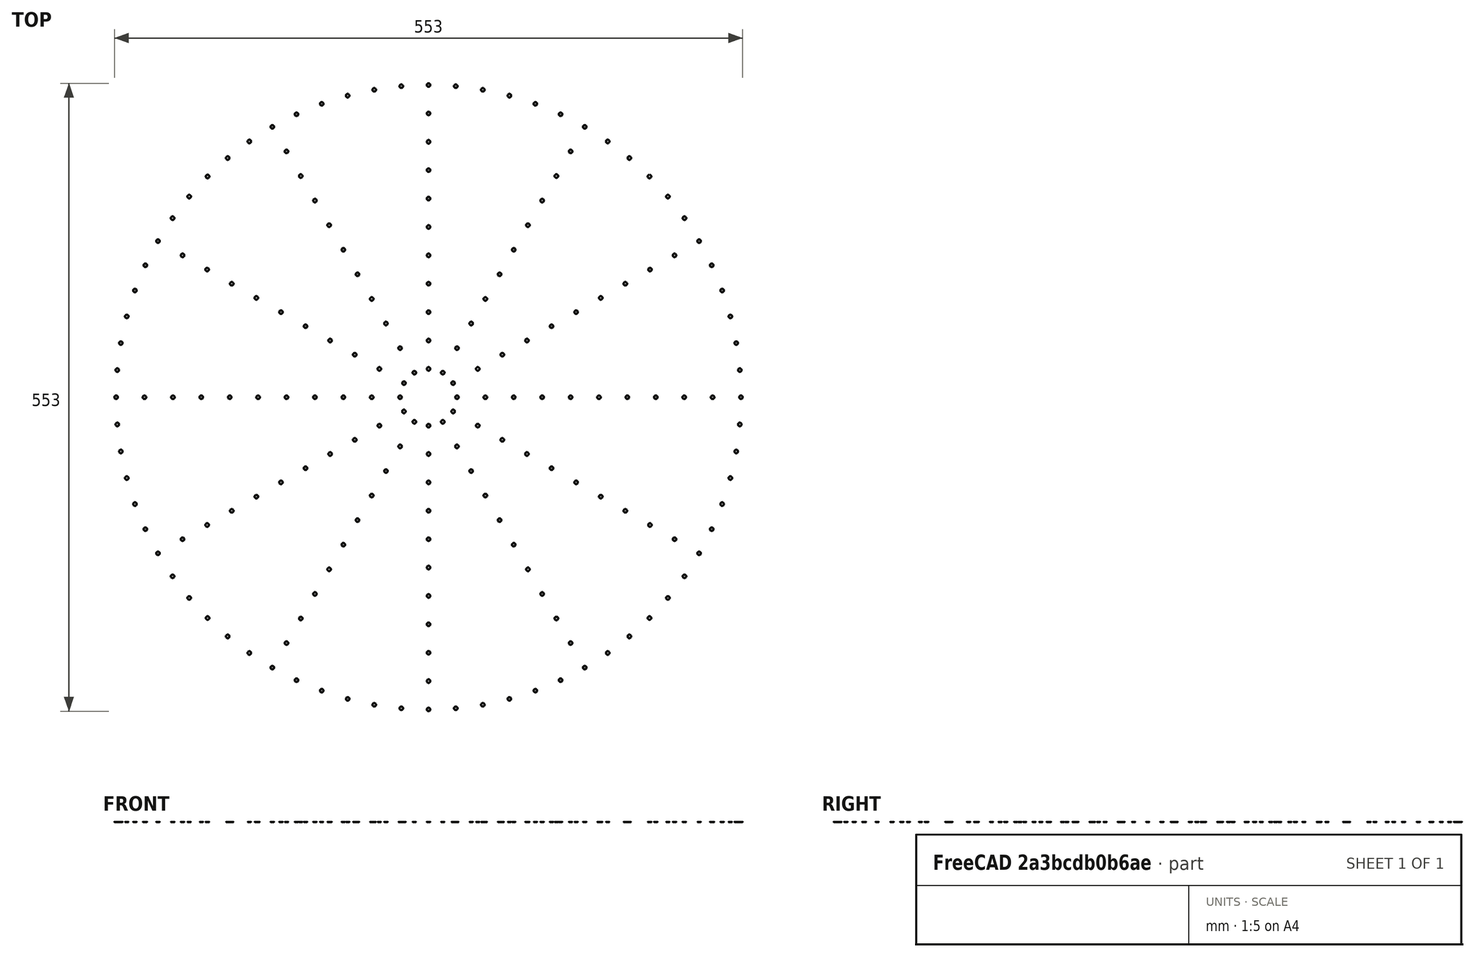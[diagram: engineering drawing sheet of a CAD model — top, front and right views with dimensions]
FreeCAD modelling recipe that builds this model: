
FCSTD DOCUMENT  (FreeCAD 0.16RUnknown)
Label: Wheel
License: All rights reserved
LicenseURL: http://en.wikipedia.org/wiki/All_rights_reserved
objects: Part::Part2DObjectPython×4, Part::FeaturePython×3, Spreadsheet::Sheet×1
note: 7 computed .brp shape members not serialized (recipe doc carries the construction recipe); baked Part::Feature solids carry a one-line shape summary decoded from their .brp

FEATURE [Part::Part2DObjectPython] Circle  label="externalCircle"  # Draft 2D object (typed FeaturePython)
  FirstAngle = 0
  LastAngle = 0
  MakeFace = true
  Radius = 280
  expr: Radius = prefs.circleExternal / 2
FEATURE [Spreadsheet::Sheet] Spreadsheet  label="prefs"
  cells = A1=External circle diameter; B1(circleExternal)=560; C1=mm; D1=name=circleExternal; A2=Holes diameter; B2(holeDiameter)=3; C2=mm; D2=name=holeDiameter; A3=Center hole diameter; B3(centerDiameter)=8; C3=mm; D3=name=circleExternal; A4=External holes diameter; B4(externalHole)=3; C4=mm; D4=name=circleExternal
FEATURE [Part::Part2DObjectPython] Circle001  label="hole"  # Draft 2D object (typed FeaturePython)
  FirstAngle = 0
  LastAngle = 0
  MakeFace = true
  Placement = pos=(0,25,0) rot=(0,0,1;0rad)
  Radius = 1.5
  expr: Radius = prefs.holeDiameter / 2
FEATURE [Part::FeaturePython] Array  label="orthoArray"  # Draft array (typed FeaturePython)
  Angle = 360
  ArrayType = 0
  Axis = (0,0,1)
  Base = -> Circle001
  Center = (0,0,0)
  Fuse = false
  IntervalAxis = (0,0,0)
  IntervalX = (1,0,0)
  IntervalY = (0,25,0)
  IntervalZ = (0,0,0)
  NumberPolar = 1
  NumberX = 1
  NumberY = 10
  NumberZ = 1
FEATURE [Part::Part2DObjectPython] Circle002  label="centerHole"  # Draft 2D object (typed FeaturePython)
  FirstAngle = 0
  LastAngle = 0
  MakeFace = true
  Placement = pos=(0,0,0) rot=(1,0,0;3.14159rad)
  Radius = 4
  expr: Radius = prefs.centerDiameter / 2
FEATURE [Part::Part2DObjectPython] Circle003  label="extHole"  # Draft 2D object (typed FeaturePython)
  FirstAngle = 0
  LastAngle = 0
  MakeFace = true
  Placement = pos=(0,275,0) rot=(1,0,0;3.14159rad)
  Radius = 1.5
  expr: Radius = prefs.externalHole / 2
FEATURE [Part::FeaturePython] Array001  label="extArray"  # Draft array (typed FeaturePython)
  Angle = 360
  ArrayType = 1
  Axis = (0,0,1)
  Base = -> Circle003
  Center = (0,0,0)
  Fuse = false
  IntervalAxis = (0,0,0)
  IntervalX = (1,0,0)
  IntervalY = (0,1,0)
  IntervalZ = (0,0,0)
  NumberPolar = 72
  NumberX = 1
  NumberY = 1
  NumberZ = 1
FEATURE [Part::FeaturePython] Array002  label="intArray"  # Draft array (typed FeaturePython)
  Angle = 360
  ArrayType = 1
  Axis = (0,0,1)
  Base = -> Array
  Center = (0,0,0)
  Fuse = false
  IntervalAxis = (0,0,0)
  IntervalX = (1,0,0)
  IntervalY = (0,1,0)
  IntervalZ = (0,0,0)
  NumberPolar = 12
  NumberX = 1
  NumberY = 2
  NumberZ = 1
